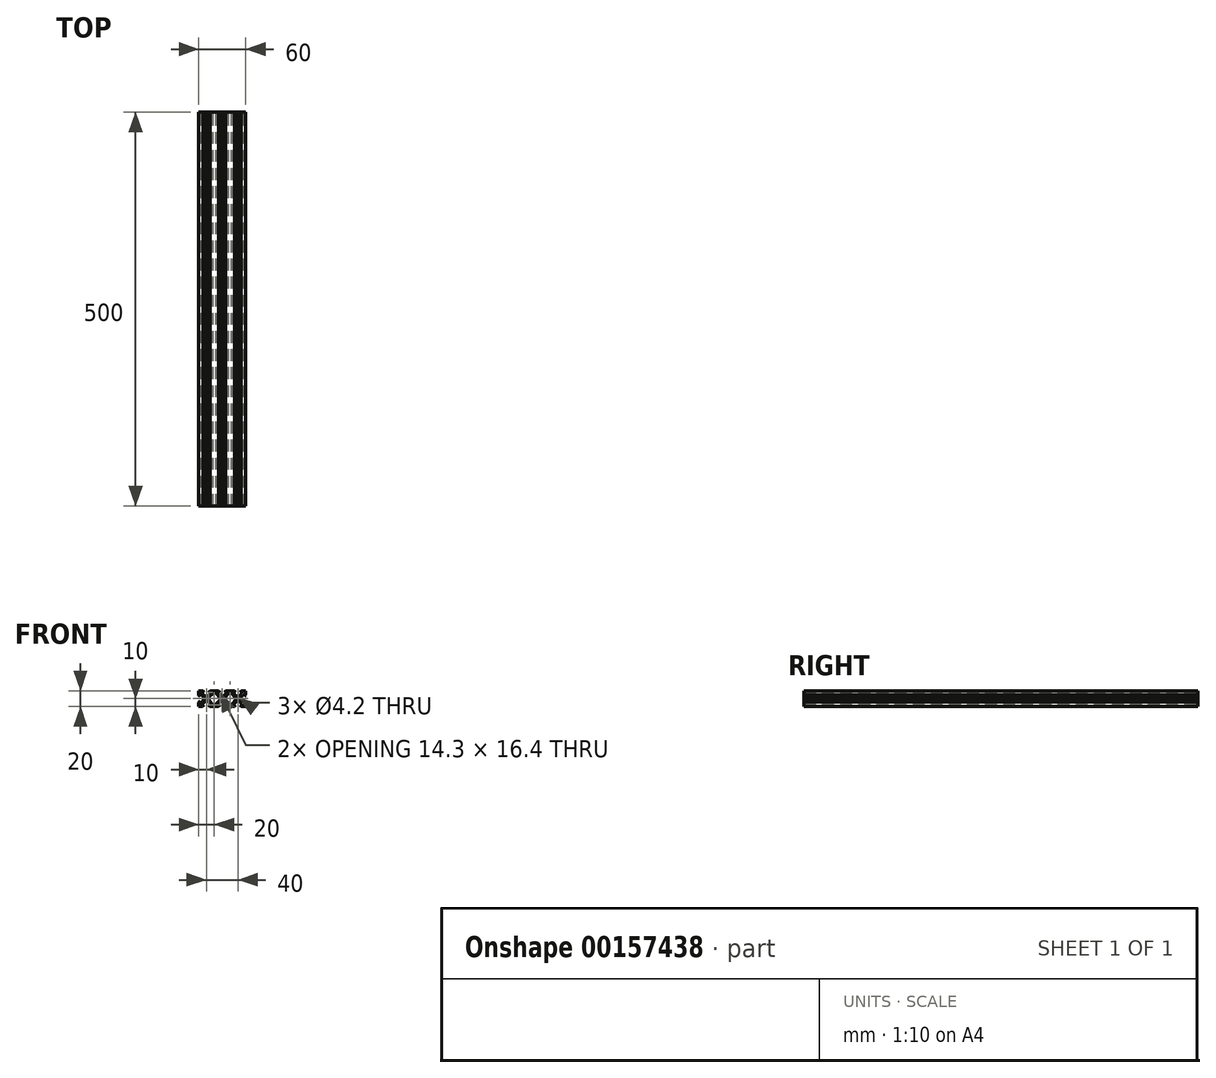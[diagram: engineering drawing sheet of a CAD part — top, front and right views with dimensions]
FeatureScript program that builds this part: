
annotation { "Feature Type Name" : "Feature", "Feature Type Description" : "" }
export const myFeature = defineFeature(function(context is Context, id is Id, definition is map)
    precondition{}
    {
        {
            var Q0;
            Q0=qCreatedBy(makeId("Front.planeOp"),FACE);
            var sketch = newSketch(context, id + "F0", { "sketchPlane" : qUnion([Q0])});
            skLineSegment(sketch, "E0.bottom", {"start": v(30, 10) * mm, "end": v(24.23, 10) * mm});
            skLineSegment(sketch, "E0.top", {"start": v(30, -10) * mm, "end": v(24.23, -10) * mm});
            skLineSegment(sketch, "E0.left", {"start": v(30, 10) * mm, "end": v(30, 4.56) * mm});
            skLineSegment(sketch, "E0.right", {"start": v(-30, 10) * mm, "end": v(-30, 4.4) * mm});
            skPoint(sketch, "E0.middle", {"position": v(0, 0) * mm});
            skLineSegment(sketch, "E1.0", {"start": v(-28.2, 8.2) * mm, "end": v(-28.2, 2.7) * mm});
            skLineSegment(sketch, "E1.1", {"start": v(28.2, 8.2) * mm, "end": v(22.92, 8.2) * mm});
            skLineSegment(sketch, "E1.2", {"start": v(28.2, 8.2) * mm, "end": v(28.2, 2.93) * mm});
            skLineSegment(sketch, "E1.3", {"start": v(28.2, -8.2) * mm, "end": v(22.78, -8.2) * mm});
            skCircle(sketch, "E2", {"center": v(0, 0) * mm, "radius": 2.1 * mm});
            skCircle(sketch, "E3", {"center": v(-20, 0) * mm, "radius": 2.1 * mm});
            skCircle(sketch, "E4", {"center": v(20, 0) * mm, "radius": 2.1 * mm});
            skLineSegment(sketch, "E5", {"start": v(-30, 4.4) * mm, "end": v(-28.2, 2.7) * mm});
            skLineSegment(sketch, "E6", {"start": v(-30, -4.47) * mm, "end": v(-28.2, -2.76) * mm});
            skLineSegment(sketch, "E7", {"start": v(-24.21, 10) * mm, "end": v(-22.7, 8.2) * mm});
            skLineSegment(sketch, "E8", {"start": v(-17.28, 8.2) * mm, "end": v(-15.53, 10) * mm});
            skLineSegment(sketch, "E9", {"start": v(-24.77, -10) * mm, "end": v(-23.06, -8.2) * mm});
            skLineSegment(sketch, "E10", {"start": v(-17.09, -8.2) * mm, "end": v(-15.66, -10) * mm});
            skLineSegment(sketch, "E11", {"start": v(2.9, 8.2) * mm, "end": v(4.22, 10) * mm});
            skLineSegment(sketch, "E12", {"start": v(-4.42, -10) * mm, "end": v(-2.88, -8.2) * mm});
            skLineSegment(sketch, "E13", {"start": v(2.82, -8.2) * mm, "end": v(4.44, -10) * mm});
            skLineSegment(sketch, "E14", {"start": v(15.72, 10) * mm, "end": v(17.27, 8.2) * mm});
            skLineSegment(sketch, "E15", {"start": v(22.92, 8.2) * mm, "end": v(24.23, 10) * mm});
            skLineSegment(sketch, "E16", {"start": v(15.6, -10) * mm, "end": v(17.12, -8.2) * mm});
            skLineSegment(sketch, "E17", {"start": v(22.78, -8.2) * mm, "end": v(24.23, -10) * mm});
            skLineSegment(sketch, "E18", {"start": v(28.2, -2.83) * mm, "end": v(30, -4) * mm});
            skLineSegment(sketch, "E19", {"start": v(28.2, 2.93) * mm, "end": v(30, 4.56) * mm});
            skLineSegment(sketch, "E20.bottom", {"start": v(-17.15, 2.85) * mm, "end": v(-22.85, 2.85) * mm});
            skLineSegment(sketch, "E20.top", {"start": v(-17.15, -2.85) * mm, "end": v(-22.85, -2.85) * mm});
            skLineSegment(sketch, "E20.left", {"start": v(-17.15, 2.85) * mm, "end": v(-17.15, -2.85) * mm});
            skLineSegment(sketch, "E20.right", {"start": v(-22.85, 2.85) * mm, "end": v(-22.85, -2.85) * mm});
            skLineSegment(sketch, "E21.bottom", {"start": v(2.85, 2.85) * mm, "end": v(-2.85, 2.85) * mm});
            skLineSegment(sketch, "E21.top", {"start": v(2.85, -2.85) * mm, "end": v(-2.85, -2.85) * mm});
            skLineSegment(sketch, "E21.left", {"start": v(2.85, 2.85) * mm, "end": v(2.85, -2.85) * mm});
            skLineSegment(sketch, "E21.right", {"start": v(-2.85, 2.85) * mm, "end": v(-2.85, -2.85) * mm});
            skLineSegment(sketch, "E22.bottom", {"start": v(22.85, 2.85) * mm, "end": v(17.15, 2.85) * mm});
            skLineSegment(sketch, "E22.top", {"start": v(22.85, -2.85) * mm, "end": v(17.15, -2.85) * mm});
            skLineSegment(sketch, "E22.left", {"start": v(22.85, 2.85) * mm, "end": v(22.85, -2.85) * mm});
            skLineSegment(sketch, "E22.right", {"start": v(17.15, 2.85) * mm, "end": v(17.15, -2.85) * mm});
            skLineSegment(sketch, "E23", {"start": v(-20, 2.1) * mm, "end": v(-44.26, 2.1) * mm, "construction": true});
            skPoint(sketch, "E23.startSnap0", {"position": v(-20, 2.85) * mm});
            skLineSegment(sketch, "E24", {"start": v(-19.99, -2.1) * mm, "end": v(-43.86, -2.1) * mm, "construction": true});
            skLineSegment(sketch, "E25.0", {"start": v(-26.56, 6.56) * mm, "end": v(-26.56, 5.27) * mm});
            skLineSegment(sketch, "E25.1", {"start": v(26.56, 6.56) * mm, "end": v(24.93, 6.56) * mm});
            skLineSegment(sketch, "E25.2", {"start": v(26.56, 6.56) * mm, "end": v(26.56, 4.88) * mm});
            skLineSegment(sketch, "E25.3", {"start": v(26.56, -6.56) * mm, "end": v(24.9, -6.56) * mm});
            skLineSegment(sketch, "E26", {"start": v(-25.2, 6.56) * mm, "end": v(-25.2, 8.2) * mm});
            skLineSegment(sketch, "E27", {"start": v(-26.56, 5.27) * mm, "end": v(-28.2, 5.27) * mm});
            skLineSegment(sketch, "E28", {"start": v(-25.2, 6.56) * mm, "end": v(-21.3, 2.85) * mm});
            skLineSegment(sketch, "E29", {"start": v(-26.56, 5.27) * mm, "end": v(-22.85, 1.46) * mm});
            skLineSegment(sketch, "E30", {"start": v(-26.56, -5.15) * mm, "end": v(-22.85, -1.11) * mm});
            skLineSegment(sketch, "E31", {"start": v(-24.9, -6.56) * mm, "end": v(-21.17, -2.85) * mm});
            skLineSegment(sketch, "E32", {"start": v(-26.56, -5.15) * mm, "end": v(-28.2, -5.15) * mm});
            skLineSegment(sketch, "E33", {"start": v(-24.9, -6.56) * mm, "end": v(-24.9, -8.2) * mm});
            skLineSegment(sketch, "E34", {"start": v(-14.86, 8.2) * mm, "end": v(-14.86, 6.56) * mm});
            skLineSegment(sketch, "E35", {"start": v(-14.86, 6.56) * mm, "end": v(-18.6, 2.85) * mm});
            skLineSegment(sketch, "E36", {"start": v(-17.15, 1.27) * mm, "end": v(-11.83, 6.56) * mm});
            skLineSegment(sketch, "E37", {"start": v(-2.77, 8.2) * mm, "end": v(-4.42, 10) * mm});
            skLineSegment(sketch, "E38", {"start": v(-18.74, -2.85) * mm, "end": v(-15.4, -6.56) * mm});
            skLineSegment(sketch, "E39", {"start": v(-15.4, -6.56) * mm, "end": v(-15.4, -8.2) * mm});
            skLineSegment(sketch, "E40", {"start": v(-17.15, -1.23) * mm, "end": v(-12.58, -6.56) * mm});
            skLineSegment(sketch, "E41", {"start": v(-1.3, 2.85) * mm, "end": v(-4.84, 6.56) * mm});
            skLineSegment(sketch, "E42", {"start": v(-4.84, 6.56) * mm, "end": v(-4.84, 8.2) * mm});
            skLineSegment(sketch, "E43", {"start": v(-2.85, 1.13) * mm, "end": v(-7.54, 6.56) * mm});
            skLineSegment(sketch, "E44", {"start": v(-2.85, -1.54) * mm, "end": v(-7.8, -6.56) * mm});
            skLineSegment(sketch, "E45", {"start": v(-1.46, -2.85) * mm, "end": v(-5.09, -6.56) * mm});
            skLineSegment(sketch, "E46", {"start": v(-5.09, -6.56) * mm, "end": v(-5.09, -8.2) * mm});
            skLineSegment(sketch, "E47", {"start": v(-12.58, -6.56) * mm, "end": v(-12.58, -8.2) * mm});
            skLineSegment(sketch, "E48", {"start": v(-7.8, -6.56) * mm, "end": v(-7.8, -8.2) * mm});
            skLineSegment(sketch, "E49", {"start": v(-7.54, 6.56) * mm, "end": v(-7.54, 8.2) * mm});
            skLineSegment(sketch, "E50", {"start": v(-11.83, 6.56) * mm, "end": v(-11.83, 8.2) * mm});
            skLineSegment(sketch, "E51", {"start": v(1.34, 2.85) * mm, "end": v(5.05, 6.56) * mm});
            skLineSegment(sketch, "E52", {"start": v(2.85, 1.12) * mm, "end": v(8, 6.56) * mm});
            skLineSegment(sketch, "E53", {"start": v(8, 6.56) * mm, "end": v(8, 8.2) * mm});
            skLineSegment(sketch, "E54", {"start": v(1.52, -2.85) * mm, "end": v(5.25, -6.56) * mm});
            skLineSegment(sketch, "E55", {"start": v(5.25, -6.5) * mm, "end": v(5.25, -8.2) * mm});
            skLineSegment(sketch, "E56", {"start": v(2.85, -1.1) * mm, "end": v(8, -6.56) * mm});
            skLineSegment(sketch, "E57", {"start": v(18.75, 2.85) * mm, "end": v(14.61, 6.56) * mm});
            skLineSegment(sketch, "E58", {"start": v(17.15, 1.18) * mm, "end": v(12.15, 6.56) * mm});
            skLineSegment(sketch, "E59", {"start": v(12.15, 6.51) * mm, "end": v(12.15, 8.2) * mm});
            skLineSegment(sketch, "E60", {"start": v(14.61, 6.56) * mm, "end": v(14.61, 8.2) * mm});
            skLineSegment(sketch, "E61", {"start": v(17.15, -1.45) * mm, "end": v(12.58, -6.56) * mm});
            skLineSegment(sketch, "E62", {"start": v(18.78, -2.85) * mm, "end": v(15.13, -6.56) * mm});
            skLineSegment(sketch, "E63", {"start": v(12.58, -6.56) * mm, "end": v(12.58, -8.2) * mm});
            skLineSegment(sketch, "E64", {"start": v(21.38, 2.85) * mm, "end": v(24.93, 6.56) * mm});
            skLineSegment(sketch, "E65", {"start": v(22.85, 1.03) * mm, "end": v(26.56, 4.88) * mm});
            skLineSegment(sketch, "E66", {"start": v(22.85, -1.37) * mm, "end": v(26.56, -4.98) * mm});
            skLineSegment(sketch, "E67", {"start": v(26.5, -4.98) * mm, "end": v(28.2, -4.98) * mm});
            skLineSegment(sketch, "E68", {"start": v(21.27, -2.85) * mm, "end": v(24.9, -6.56) * mm});
            skLineSegment(sketch, "E69", {"start": v(24.9, -6.5) * mm, "end": v(24.9, -8.2) * mm});
            skLineSegment(sketch, "E70.trimOffspring", {"start": v(-24.21, 10) * mm, "end": v(-30, 10) * mm});
            skLineSegment(sketch, "E71.trimOffspring", {"start": v(-22.7, 8.2) * mm, "end": v(-28.2, 8.2) * mm});
            skLineSegment(sketch, "E72.trimOffspring", {"start": v(-25.2, 6.56) * mm, "end": v(-26.56, 6.56) * mm});
            skLineSegment(sketch, "E73.trimOffspring", {"start": v(-28.2, -2.76) * mm, "end": v(-28.2, -8.2) * mm});
            skLineSegment(sketch, "E74.trimOffspring", {"start": v(-30, -4.47) * mm, "end": v(-30, -10) * mm});
            skLineSegment(sketch, "E75.trimOffspring", {"start": v(-26.56, -5.15) * mm, "end": v(-26.56, -6.56) * mm});
            skLineSegment(sketch, "E76.trimOffspring", {"start": v(-11.83, 6.56) * mm, "end": v(-14.86, 6.56) * mm});
            skLineSegment(sketch, "E77.trimOffspring", {"start": v(-12.58, -6.56) * mm, "end": v(-15.4, -6.56) * mm});
            skLineSegment(sketch, "E78.trimOffspring", {"start": v(-24.9, -6.56) * mm, "end": v(-26.56, -6.56) * mm});
            skLineSegment(sketch, "E79.trimOffspring", {"start": v(-23.06, -8.2) * mm, "end": v(-28.2, -8.2) * mm});
            skLineSegment(sketch, "E80.trimOffspring", {"start": v(-24.77, -10) * mm, "end": v(-30, -10) * mm});
            skLineSegment(sketch, "E81.trimOffspring", {"start": v(-4.42, 10) * mm, "end": v(-15.53, 10) * mm});
            skLineSegment(sketch, "E82", {"start": v(5.05, 6.56) * mm, "end": v(5.05, 8.2) * mm});
            skLineSegment(sketch, "E83.trimOffspring", {"start": v(-2.77, 8.2) * mm, "end": v(-17.28, 8.2) * mm});
            skLineSegment(sketch, "E84.trimOffspring", {"start": v(-4.84, 6.56) * mm, "end": v(-7.54, 6.56) * mm});
            skLineSegment(sketch, "E85.trimOffspring", {"start": v(8, 6.56) * mm, "end": v(5.05, 6.56) * mm});
            skLineSegment(sketch, "E86.trimOffspring", {"start": v(8, -6.56) * mm, "end": v(5.25, -6.56) * mm});
            skLineSegment(sketch, "E87.trimOffspring", {"start": v(-4.42, -10) * mm, "end": v(-15.66, -10) * mm});
            skLineSegment(sketch, "E88.trimOffspring", {"start": v(-2.88, -8.2) * mm, "end": v(-17.09, -8.2) * mm});
            skLineSegment(sketch, "E89.trimOffspring", {"start": v(-5.09, -6.56) * mm, "end": v(-7.8, -6.56) * mm});
            skLineSegment(sketch, "E90.trimOffspring", {"start": v(15.6, -10) * mm, "end": v(4.44, -10) * mm});
            skLineSegment(sketch, "E91", {"start": v(15.13, -6.56) * mm, "end": v(15.13, -8.2) * mm});
            skLineSegment(sketch, "E92.trimOffspring", {"start": v(17.12, -8.2) * mm, "end": v(2.82, -8.2) * mm});
            skLineSegment(sketch, "E93.trimOffspring", {"start": v(15.13, -6.56) * mm, "end": v(12.58, -6.56) * mm});
            skLineSegment(sketch, "E94.trimOffspring", {"start": v(30, -4) * mm, "end": v(30, -10) * mm});
            skLineSegment(sketch, "E95.trimOffspring", {"start": v(28.2, -2.83) * mm, "end": v(28.2, -8.2) * mm});
            skLineSegment(sketch, "E96.trimOffspring", {"start": v(26.56, -4.98) * mm, "end": v(26.56, -6.56) * mm});
            skLineSegment(sketch, "E97", {"start": v(24.93, 6.56) * mm, "end": v(24.93, 8.2) * mm});
            skLineSegment(sketch, "E98", {"start": v(26.56, 4.88) * mm, "end": v(28.2, 4.88) * mm});
            skLineSegment(sketch, "E99.trimOffspring", {"start": v(15.72, 10) * mm, "end": v(4.22, 10) * mm});
            skLineSegment(sketch, "E100.trimOffspring", {"start": v(17.27, 8.2) * mm, "end": v(2.9, 8.2) * mm});
            skLineSegment(sketch, "E101.trimOffspring", {"start": v(14.61, 6.56) * mm, "end": v(12.15, 6.56) * mm});
            skLineSegment(sketch, "E102", {"start": v(8, -6.56) * mm, "end": v(8, -8.2) * mm});
            skSolve(sketch);
        }
        {
            var Q0;
            Q0=makeQuery(id+"F0.imprint","IMPRINT",FACE,{"disambiguationData":[TD([[makeQuery(id+"F0.imprint","IMPRINT",EDGE,{"derivedFrom":sQuery(id+"F0.wireOp",EDGE,"E0.bottom")}),1.0]])]});
            var Q1;
            Q1=makeQuery(id+"F0.imprint","IMPRINT",FACE,{"disambiguationData":[TD([[makeQuery(id+"F0.imprint","IMPRINT",EDGE,{"derivedFrom":sQuery(id+"F0.wireOp",EDGE,"E25.1")}),-1.0]])]});
            var Q2;
            Q2=makeQuery(id+"F0.imprint","IMPRINT",FACE,{"disambiguationData":[TD([[makeQuery(id+"F0.imprint","IMPRINT",EDGE,{"derivedFrom":sQuery(id+"F0.wireOp",EDGE,"E25.1")}),1.0]])]});
            var Q3;
            {var subQ1=sQuery(id+"F0.wireOp",EDGE,"E25.3");Q3=makeQuery(id+"F0.imprint","IMPRINT",FACE,{"disambiguationData":[TD([[makeQuery(id+"F0.imprint","IMPRINT",EDGE,{"derivedFrom":subQ1}),1.0]])]});}
            var Q4;
            Q4=makeQuery(id+"F0.imprint","IMPRINT",FACE,{"disambiguationData":[TD([[makeQuery(id+"F0.imprint","IMPRINT",EDGE,{"derivedFrom":sQuery(id+"F0.wireOp",EDGE,"E0.top")}),-1.0]])]});
            var Q5;
            Q5=makeQuery(id+"F0.imprint","IMPRINT",FACE,{"disambiguationData":[TD([[makeQuery(id+"F0.imprint","IMPRINT",EDGE,{"derivedFrom":sQuery(id+"F0.wireOp",EDGE,"E25.3")}),-1.0]])]});
            var Q6;
            Q6=makeQuery(id+"F0.imprint","IMPRINT",FACE,{"disambiguationData":[TD([[makeQuery(id+"F0.imprint","IMPRINT",EDGE,{"derivedFrom":sQuery(id+"F0.wireOp",EDGE,"E4")}),-1.0]])]});
            var Q7;
            {var subQ1=sQuery(id+"F0.wireOp",EDGE,"E57");Q7=makeQuery(id+"F0.imprint","IMPRINT",FACE,{"disambiguationData":[TD([[makeQuery(id+"F0.imprint","IMPRINT",EDGE,{"derivedFrom":subQ1}),1.0]])]});}
            var Q8;
            {var subQ4=sQuery(id+"F0.wireOp",EDGE,"E60");Q8=makeQuery(id+"F0.imprint","IMPRINT",FACE,{"disambiguationData":[TD([[makeQuery(id+"F0.imprint","IMPRINT",EDGE,{"derivedFrom":subQ4}),1.0]])]});}
            var Q9;
            {var subQ3=sQuery(id+"F0.wireOp",EDGE,"E11");Q9=makeQuery(id+"F0.imprint","IMPRINT",FACE,{"disambiguationData":[TD([[makeQuery(id+"F0.imprint","IMPRINT",EDGE,{"derivedFrom":subQ3}),-1.0]])]});}
            var Q10;
            {var subQ0=sQuery(id+"F0.wireOp",EDGE,"E53");Q10=makeQuery(id+"F0.imprint","IMPRINT",FACE,{"disambiguationData":[TD([[makeQuery(id+"F0.imprint","IMPRINT",EDGE,{"derivedFrom":subQ0}),1.0]])]});}
            var Q11;
            {var subQ1=sQuery(id+"F0.wireOp",EDGE,"E51");Q11=makeQuery(id+"F0.imprint","IMPRINT",FACE,{"disambiguationData":[TD([[makeQuery(id+"F0.imprint","IMPRINT",EDGE,{"derivedFrom":subQ1}),-1.0]])]});}
            var Q12;
            {var subQ4=sQuery(id+"F0.wireOp",EDGE,"E61");Q12=makeQuery(id+"F0.imprint","IMPRINT",FACE,{"disambiguationData":[TD([[makeQuery(id+"F0.imprint","IMPRINT",EDGE,{"derivedFrom":subQ4}),1.0]])]});}
            var Q13;
            {var subQ0=sQuery(id+"F0.wireOp",EDGE,"E63");Q13=makeQuery(id+"F0.imprint","IMPRINT",FACE,{"disambiguationData":[TD([[makeQuery(id+"F0.imprint","IMPRINT",EDGE,{"derivedFrom":subQ0}),1.0]])]});}
            var Q14;
            {var subQ3=sQuery(id+"F0.wireOp",EDGE,"E13");Q14=makeQuery(id+"F0.imprint","IMPRINT",FACE,{"disambiguationData":[TD([[makeQuery(id+"F0.imprint","IMPRINT",EDGE,{"derivedFrom":subQ3}),1.0]])]});}
            var Q15;
            {var subQ0=sQuery(id+"F0.wireOp",EDGE,"E86.trimOffspring");Q15=makeQuery(id+"F0.imprint","IMPRINT",FACE,{"disambiguationData":[TD([[makeQuery(id+"F0.imprint","IMPRINT",EDGE,{"derivedFrom":subQ0}),1.0]])]});}
            var Q16;
            {var subQ1=sQuery(id+"F0.wireOp",EDGE,"E54");Q16=makeQuery(id+"F0.imprint","IMPRINT",FACE,{"disambiguationData":[TD([[makeQuery(id+"F0.imprint","IMPRINT",EDGE,{"derivedFrom":subQ1}),1.0]])]});}
            var Q17;
            Q17=makeQuery(id+"F0.imprint","IMPRINT",FACE,{"disambiguationData":[TD([[makeQuery(id+"F0.imprint","IMPRINT",EDGE,{"derivedFrom":sQuery(id+"F0.wireOp",EDGE,"E2")}),-1.0]])]});
            var Q18;
            {var subQ0=sQuery(id+"F0.wireOp",EDGE,"E41");Q18=makeQuery(id+"F0.imprint","IMPRINT",FACE,{"disambiguationData":[TD([[makeQuery(id+"F0.imprint","IMPRINT",EDGE,{"derivedFrom":subQ0}),1.0]])]});}
            var Q19;
            {var subQ0=sQuery(id+"F0.wireOp",EDGE,"E42");Q19=makeQuery(id+"F0.imprint","IMPRINT",FACE,{"disambiguationData":[TD([[makeQuery(id+"F0.imprint","IMPRINT",EDGE,{"derivedFrom":subQ0}),1.0]])]});}
            var Q20;
            {var subQ5=sQuery(id+"F0.wireOp",EDGE,"E8");Q20=makeQuery(id+"F0.imprint","IMPRINT",FACE,{"disambiguationData":[TD([[makeQuery(id+"F0.imprint","IMPRINT",EDGE,{"derivedFrom":subQ5}),-1.0]])]});}
            var Q21;
            {var subQ0=sQuery(id+"F0.wireOp",EDGE,"E34");Q21=makeQuery(id+"F0.imprint","IMPRINT",FACE,{"disambiguationData":[TD([[makeQuery(id+"F0.imprint","IMPRINT",EDGE,{"derivedFrom":subQ0}),1.0]])]});}
            var Q22;
            {var subQ0=sQuery(id+"F0.wireOp",EDGE,"E35");Q22=makeQuery(id+"F0.imprint","IMPRINT",FACE,{"disambiguationData":[TD([[makeQuery(id+"F0.imprint","IMPRINT",EDGE,{"derivedFrom":subQ0}),1.0]])]});}
            var Q23;
            {var subQ1=sQuery(id+"F0.wireOp",EDGE,"E44");Q23=makeQuery(id+"F0.imprint","IMPRINT",FACE,{"disambiguationData":[TD([[makeQuery(id+"F0.imprint","IMPRINT",EDGE,{"derivedFrom":subQ1}),1.0]])]});}
            var Q24;
            {var subQ0=sQuery(id+"F0.wireOp",EDGE,"E46");Q24=makeQuery(id+"F0.imprint","IMPRINT",FACE,{"disambiguationData":[TD([[makeQuery(id+"F0.imprint","IMPRINT",EDGE,{"derivedFrom":subQ0}),-1.0]])]});}
            var Q25;
            {var subQ3=sQuery(id+"F0.wireOp",EDGE,"E10");Q25=makeQuery(id+"F0.imprint","IMPRINT",FACE,{"disambiguationData":[TD([[makeQuery(id+"F0.imprint","IMPRINT",EDGE,{"derivedFrom":subQ3}),1.0]])]});}
            var Q26;
            {var subQ0=sQuery(id+"F0.wireOp",EDGE,"E39");Q26=makeQuery(id+"F0.imprint","IMPRINT",FACE,{"disambiguationData":[TD([[makeQuery(id+"F0.imprint","IMPRINT",EDGE,{"derivedFrom":subQ0}),1.0]])]});}
            var Q27;
            {var subQ0=sQuery(id+"F0.wireOp",EDGE,"E38");Q27=makeQuery(id+"F0.imprint","IMPRINT",FACE,{"disambiguationData":[TD([[makeQuery(id+"F0.imprint","IMPRINT",EDGE,{"derivedFrom":subQ0}),1.0]])]});}
            var Q28;
            Q28=makeQuery(id+"F0.imprint","IMPRINT",FACE,{"disambiguationData":[TD([[makeQuery(id+"F0.imprint","IMPRINT",EDGE,{"derivedFrom":sQuery(id+"F0.wireOp",EDGE,"E3")}),-1.0]])]});
            var Q29;
            Q29=makeQuery(id+"F0.imprint","IMPRINT",FACE,{"disambiguationData":[TD([[makeQuery(id+"F0.imprint","IMPRINT",EDGE,{"derivedFrom":sQuery(id+"F0.wireOp",EDGE,"E25.0")}),1.0]])]});
            var Q30;
            {var subQ1=sQuery(id+"F0.wireOp",EDGE,"E30");Q30=makeQuery(id+"F0.imprint","IMPRINT",FACE,{"disambiguationData":[TD([[makeQuery(id+"F0.imprint","IMPRINT",EDGE,{"derivedFrom":subQ1}),-1.0]])]});}
            var Q31;
            Q31=makeQuery(id+"F0.imprint","IMPRINT",FACE,{"disambiguationData":[TD([[makeQuery(id+"F0.imprint","IMPRINT",EDGE,{"derivedFrom":sQuery(id+"F0.wireOp",EDGE,"E25.0")}),-1.0]])]});
            var Q32;
            Q32=makeQuery(id+"F0.imprint","IMPRINT",FACE,{"disambiguationData":[TD([[makeQuery(id+"F0.imprint","IMPRINT",EDGE,{"derivedFrom":sQuery(id+"F0.wireOp",EDGE,"E0.right")}),1.0]])]});
            var Q33;
            {var subQ1=sQuery(id+"F0.wireOp",EDGE,"E32");Q33=makeQuery(id+"F0.imprint","IMPRINT",FACE,{"disambiguationData":[TD([[makeQuery(id+"F0.imprint","IMPRINT",EDGE,{"derivedFrom":subQ1}),1.0]])]});}
            var Q34;
            {var subQ4=sQuery(id+"F0.wireOp",EDGE,"E6");Q34=makeQuery(id+"F0.imprint","IMPRINT",FACE,{"disambiguationData":[TD([[makeQuery(id+"F0.imprint","IMPRINT",EDGE,{"derivedFrom":subQ4}),-1.0]])]});}
            extrude(context, id + "F1", {"entities" : qUnion([Q0, Q1, Q2, Q3, Q4, Q5, Q6, Q7, Q8, Q9, Q10, Q11, Q12, Q13, Q14, Q15, Q16, Q17, Q18, Q19, Q20, Q21, Q22, Q23, Q24, Q25, Q26, Q27, Q28, Q29, Q30, Q31, Q32, Q33, Q34]), "depth" : 500 * mm});
        }
    });
